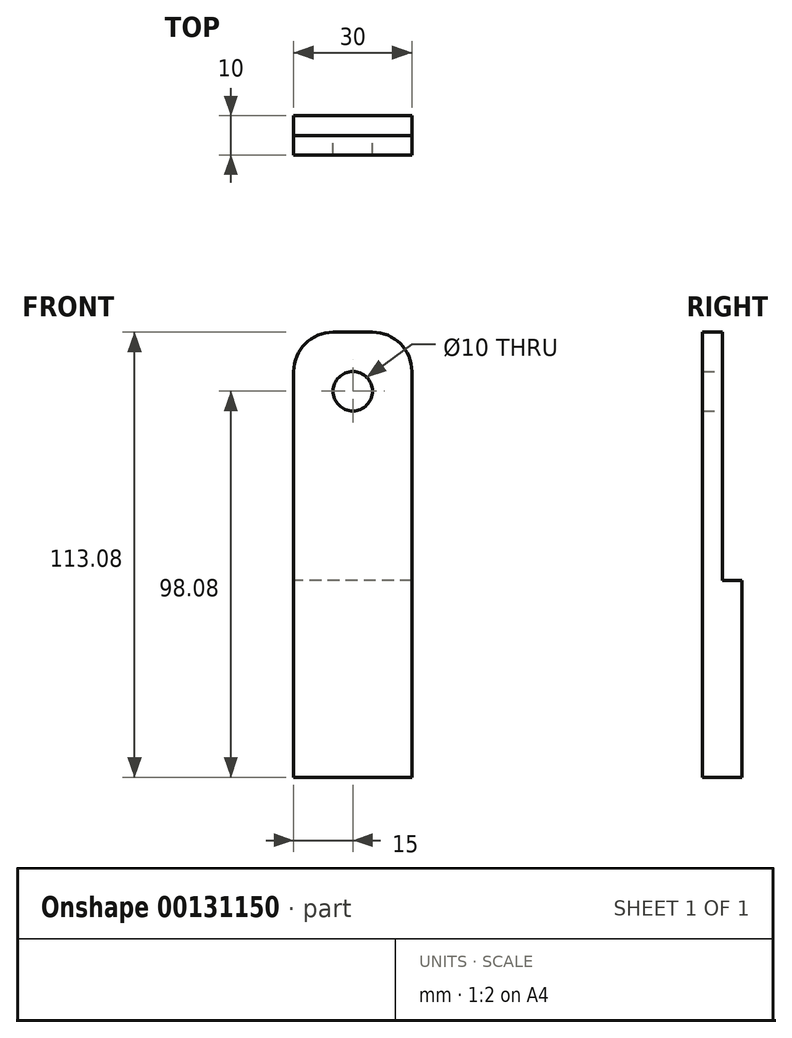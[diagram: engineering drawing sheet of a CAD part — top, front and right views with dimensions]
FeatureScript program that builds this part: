
annotation { "Feature Type Name" : "Feature", "Feature Type Description" : "" }
export const myFeature = defineFeature(function(context is Context, id is Id, definition is map)
    precondition{}
    {
        {
            var Q0;
            Q0=qCreatedBy(makeId("Front.planeOp"),FACE);
            var sketch = newSketch(context, id + "F0", { "sketchPlane" : qUnion([Q0])});
            skLineSegment(sketch, "E0.bottom", {"start": v(15, 56.54) * mm, "end": v(-15, 56.54) * mm});
            skLineSegment(sketch, "E0.top", {"start": v(15, -56.54) * mm, "end": v(-15, -56.54) * mm});
            skLineSegment(sketch, "E0.left", {"start": v(15, 56.54) * mm, "end": v(15, -56.54) * mm});
            skLineSegment(sketch, "E0.right", {"start": v(-15, 56.54) * mm, "end": v(-15, -56.54) * mm});
            skPoint(sketch, "E0.middle", {"position": v(0, 0) * mm});
            skCircle(sketch, "E1", {"center": v(0, 41.54) * mm, "radius": 5 * mm});
            skSolve(sketch);
        }
        {
            var Q0;
            Q0=makeQuery(id+"F0.imprint","IMPRINT",FACE,{"disambiguationData":[TD([[makeQuery(id+"F0.imprint","IMPRINT",EDGE,{"derivedFrom":sQuery(id+"F0.wireOp",EDGE,"E0.bottom")}),1.0]])]});
            extrude(context, id + "F1", {"entities" : qUnion([Q0]), "depth" : 5 * mm});
        }
        {
            var Q0;
            Q0=makeQuery(id+"F1.opExtrude","SWEPT_EDGE",EDGE,{"disambiguationData":[OSD([sQuery(id+"F0.wireOp",EDGE,"E0.bottom"),sQuery(id+"F0.wireOp",EDGE,"E0.left")])]});
            var Q1;
            Q1=makeQuery(id+"F1.opExtrude","SWEPT_EDGE",EDGE,{"disambiguationData":[OSD([sQuery(id+"F0.wireOp",EDGE,"E0.bottom"),sQuery(id+"F0.wireOp",EDGE,"E0.right")])]});
            fillet(context, id + "F2", {"entities" : qUnion([Q0, Q1]), "radius" : 10 * mm, "tangentPropagation" : true, "allowEdgeOverflow" : false});
        }
        {
            var Q0;
            Q0=makeQuery(id+"F1.opExtrude","CAP_FACE",FACE,{"disambiguationData":[OSD([sQuery(id+"F0.wireOp",EDGE,"E0.bottom"),sQuery(id+"F0.wireOp",EDGE,"E0.top"),sQuery(id+"F0.wireOp",EDGE,"E0.left"),sQuery(id+"F0.wireOp",EDGE,"E0.right"),sQuery(id+"F0.wireOp",EDGE,"E1")])],"isStart":true});
            var sketch = newSketch(context, id + "F3", { "sketchPlane" : qUnion([Q0])});
            skLineSegment(sketch, "E2.bottom", {"start": v(-15, -56.54) * mm, "end": v(15, -56.54) * mm});
            skLineSegment(sketch, "E2.top", {"start": v(-15, -6.54) * mm, "end": v(15, -6.54) * mm});
            skLineSegment(sketch, "E2.left", {"start": v(-15, -56.54) * mm, "end": v(-15, -6.54) * mm});
            skLineSegment(sketch, "E2.right", {"start": v(15, -56.54) * mm, "end": v(15, -6.54) * mm});
            skSolve(sketch);
        }
        {
            var Q0;
            Q0=makeQuery(id+"F3.imprint","IMPRINT",FACE,{"disambiguationData":[TD([[makeQuery(id+"F3.imprint","IMPRINT",EDGE,{"derivedFrom":sQuery(id+"F3.wireOp",EDGE,"E2.bottom")}),1.0]])]});
            extrude(context, id + "F4", {"entities" : qUnion([Q0]), "operationType" : NewBodyOperationType.ADD, "depth" : 5 * mm});
        }
    });
